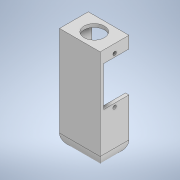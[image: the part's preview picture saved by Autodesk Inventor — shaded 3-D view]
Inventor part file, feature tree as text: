
AUTODESK INVENTOR PART (.ipt)
format: ipt  version: 2022.2 (Build 262287010, 287A)  size: 203,776 bytes
history: native  units: mm
features: extrude x10, sketch x10, fillet x1
ambient origin geometry x8: Origin, YZ Plane, XZ Plane, XY Plane, X Axis, Y Axis, Z Axis, Center Point
bodies: Solid1 (feature_tree)
feature tree (21):
  extrude  "Extrusion1"  Depth=24.0mm
  extrude  "Extrusion2"  Depth=2.0mm
  extrude  "Extrusion3"  Depth=15.0mm TaperAngle=0.0deg
  extrude  "Extrusion4"  Depth=2.0mm
  extrude  "Extrusion5"  Depth=8.5mm
  extrude  "Extrusion6"  Depth=3.0mm
  extrude  "Extrusion7"  Depth=15.0mm
  extrude  "Extrusion8"  Depth=2.0mm
  extrude  "Extrusion9"  Depth=15.0mm TaperAngle=0.0deg
  fillet  "Fillet1"  Radius=5.0mm
  extrude  "Extrusion10"  Depth=2.0mm
  sketch  "Sketch1"  dims[d0=24.0mm d1=60.0mm]
  sketch  "Sketch2"  dims[d2=2.0mm d3=0.0mm d4=2.0mm]
  sketch  "Sketch3"  dims[d5=2.0mm d6=15.0mm d7=0.0mm]
  sketch  "Sketch4"  dims[d8=2.0mm d9=2.0mm]
  sketch  "Sketch5"  dims[d10=8.5mm d11=8.5mm]
  sketch  "Sketch6"  dims[d12=27.5mm d13=3.0mm]
  sketch  "Sketch7"  dims[d14=12.0mm d15=0.0mm d23=15.0mm]
  sketch  "Sketch8"  dims[d24=23.5mm d25=2.0mm]
  sketch  "Sketch9"  dims[d26=2.0mm d27=15.0mm d28=0.0mm d29=5.0mm]
  sketch  "Sketch10"  dims[d30=5.0mm d31=0.0mm d32=8.6mm d33=0.0mm d34=2.0mm d35=15.0mm d36=0.0mm d37=10.0mm d38=0.0mm d39=10.5mm d40=0.0mm d41=2.0mm d42=0.0mm d44=8.5mm d45=12.0mm d46=12.0mm d47=8.5mm d48=2.0mm d49=0.0mm]
